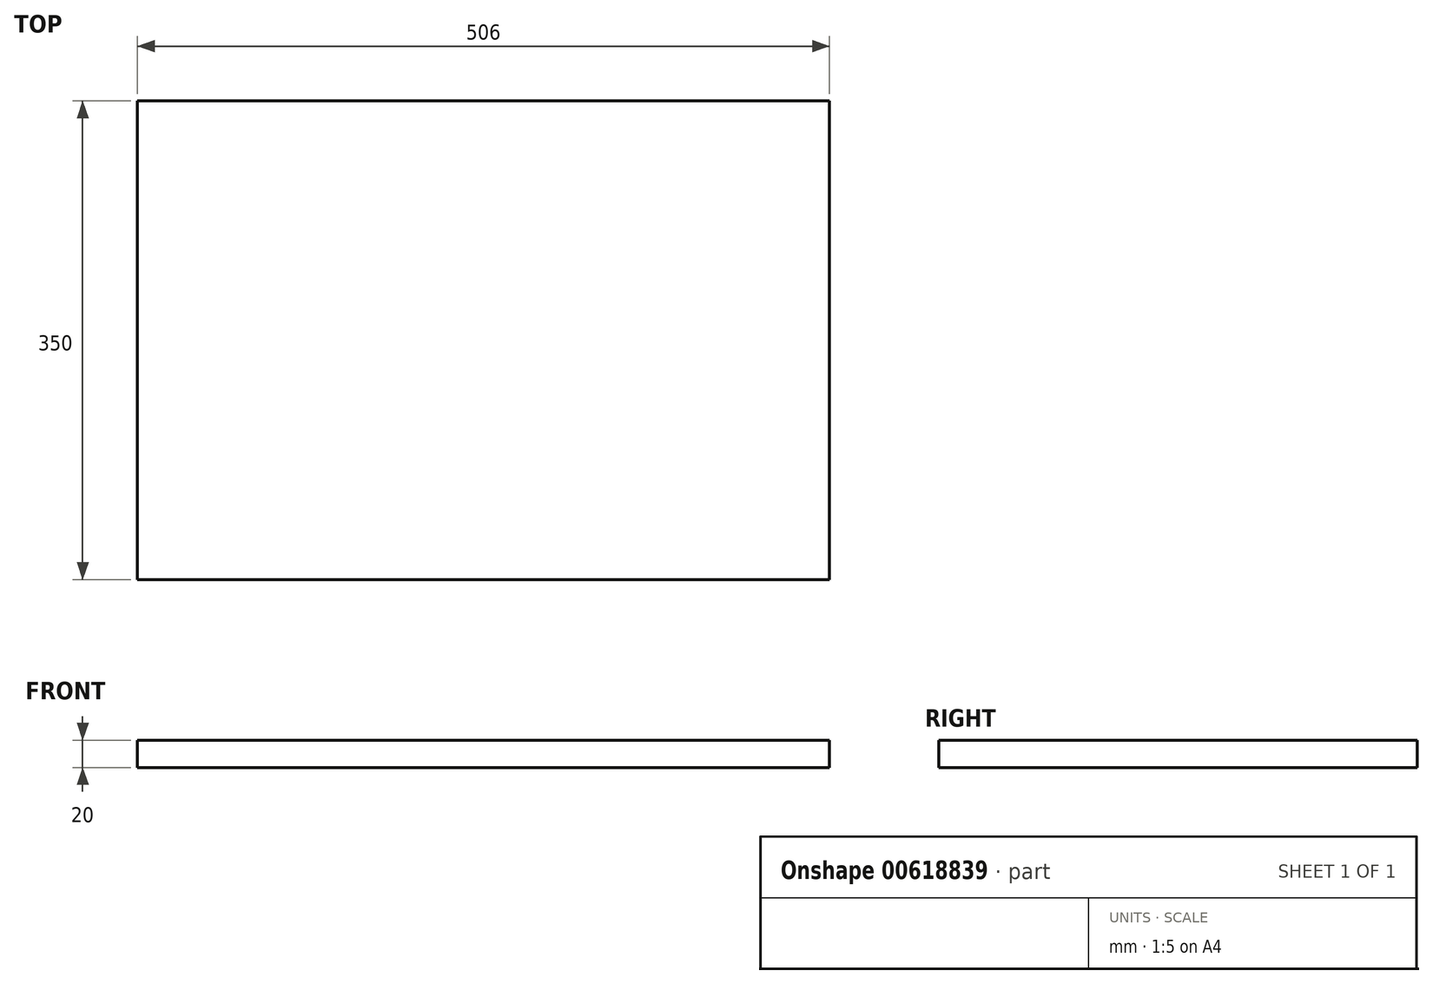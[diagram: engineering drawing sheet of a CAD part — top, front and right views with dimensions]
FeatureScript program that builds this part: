
annotation { "Feature Type Name" : "Feature", "Feature Type Description" : "" }
export const myFeature = defineFeature(function(context is Context, id is Id, definition is map)
    precondition{}
    {
        {
            var Q0;
            Q0=qCreatedBy(makeId("Top.planeOp"),FACE);
            var sketch = newSketch(context, id + "F0", { "sketchPlane" : qUnion([Q0])});
            skLineSegment(sketch, "E0.bottom", {"start": v(-253, 175) * mm, "end": v(253, 175) * mm});
            skLineSegment(sketch, "E0.top", {"start": v(-253, -175) * mm, "end": v(253, -175) * mm});
            skLineSegment(sketch, "E0.left", {"start": v(-253, 175) * mm, "end": v(-253, -175) * mm});
            skLineSegment(sketch, "E0.right", {"start": v(253, 175) * mm, "end": v(253, -175) * mm});
            skPoint(sketch, "E0.middle", {"position": v(0, 0) * mm});
            skSolve(sketch);
        }
        {
            var Q0;
            Q0 = qSketchRegion(id + "F0", true);
            extrude(context, id + "F1", {"entities" : qUnion([Q0]), "depth" : 20 * mm, "offsetDistance" : 25 * mm});
        }
    });
